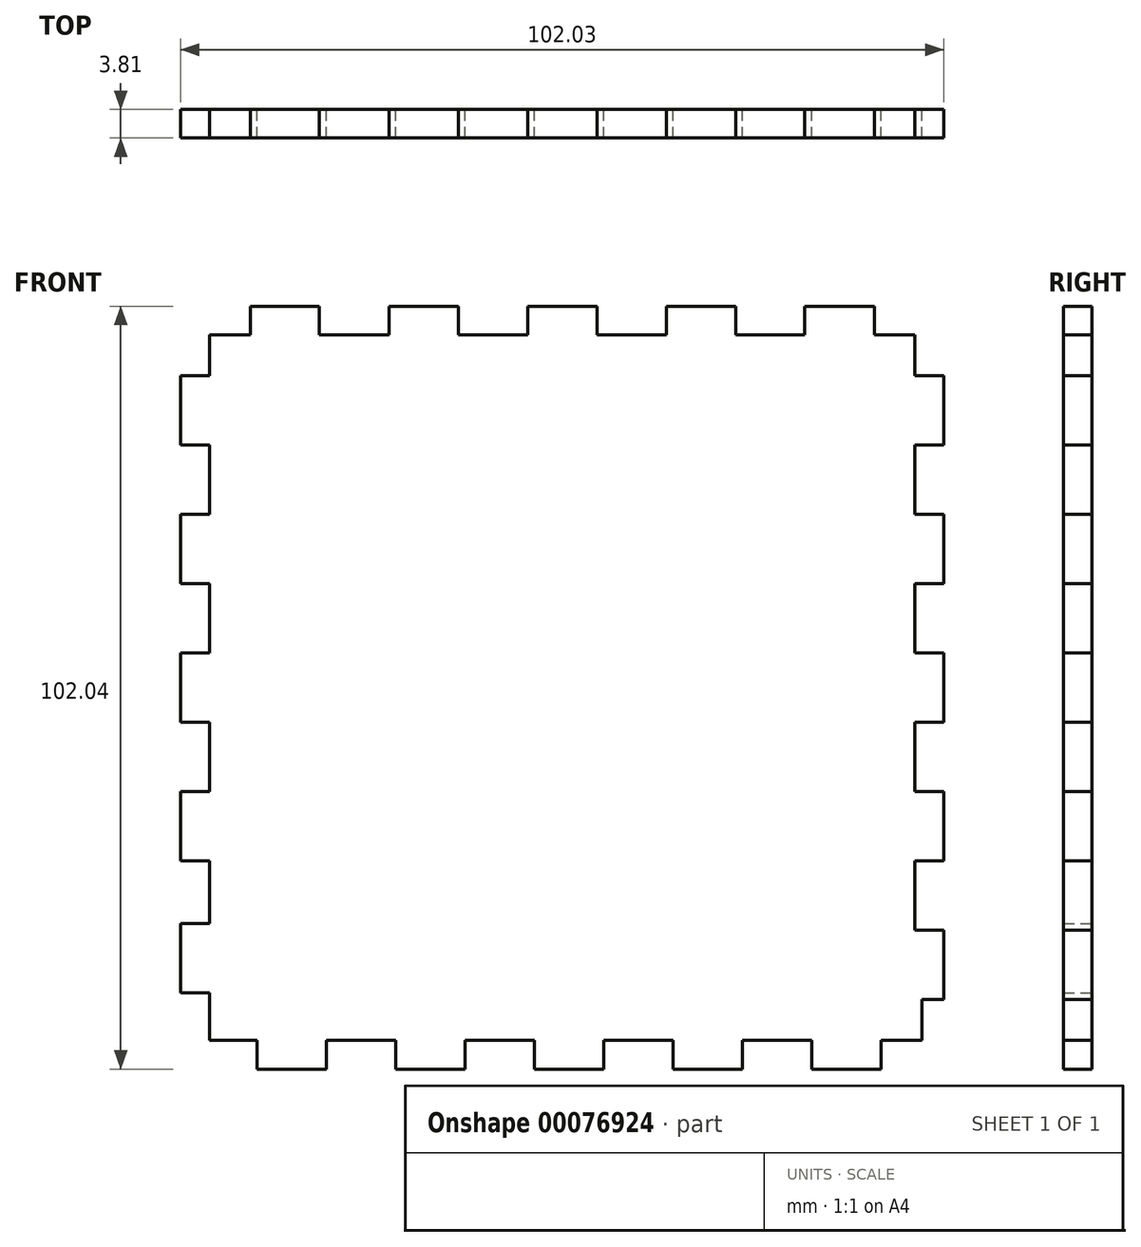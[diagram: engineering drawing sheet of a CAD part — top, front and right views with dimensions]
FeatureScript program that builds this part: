
annotation { "Feature Type Name" : "Feature", "Feature Type Description" : "" }
export const myFeature = defineFeature(function(context is Context, id is Id, definition is map)
    precondition{}
    {
        {
            var Q0;
            Q0=qCreatedBy(makeId("Front.planeOp"),FACE);
            var sketch = newSketch(context, id + "F0", { "sketchPlane" : qUnion([Q0])});
            skLineSegment(sketch, "E0.MirrorCS", {"start": v(-47.6, 5.44) * mm, "end": v(-51.43, 5.44) * mm});
            skLineSegment(sketch, "E1.MirrorCS", {"start": v(-51.43, -40) * mm, "end": v(-47.6, -40) * mm});
            skLineSegment(sketch, "E2.MirrorCS", {"start": v(-47.6, -30.73) * mm, "end": v(-51.43, -30.73) * mm});
            skLineSegment(sketch, "E3.MirrorCS", {"start": v(-51.43, -22.38) * mm, "end": v(-47.6, -22.38) * mm});
            skLineSegment(sketch, "E4.MirrorCS", {"start": v(-47.6, -13.1) * mm, "end": v(-51.43, -13.1) * mm});
            skLineSegment(sketch, "E5.MirrorCS", {"start": v(-51.43, -3.84) * mm, "end": v(-47.6, -3.84) * mm});
            skLineSegment(sketch, "E6.MirrorCS", {"start": v(-51.43, -13.1) * mm, "end": v(-51.43, -22.38) * mm});
            skLineSegment(sketch, "E7.MirrorCS", {"start": v(-47.6, -22.38) * mm, "end": v(-47.6, -30.73) * mm});
            skLineSegment(sketch, "E8.MirrorCS", {"start": v(-47.6, -40) * mm, "end": v(-47.6, -46.38) * mm});
            skLineSegment(sketch, "E9.MirrorCS", {"start": v(-51.43, -30.73) * mm, "end": v(-51.43, -40) * mm});
            skPoint(sketch, "E10.MirrorP", {"position": v(-51.43, -17.74) * mm});
            skLineSegment(sketch, "E11.MirrorCS", {"start": v(-47.6, -3.84) * mm, "end": v(-47.6, -13.1) * mm});
            skLineSegment(sketch, "E12.MirrorCS", {"start": v(-51.43, 5.44) * mm, "end": v(-51.43, -3.84) * mm});
            skLineSegment(sketch, "E13", {"start": v(-47.6, -46.38) * mm, "end": v(-41.22, -46.38) * mm});
            skLineSegment(sketch, "E14", {"start": v(-41.22, -46.38) * mm, "end": v(-41.22, -50.22) * mm});
            skLineSegment(sketch, "E15", {"start": v(-41.22, -50.22) * mm, "end": v(-31.95, -50.22) * mm});
            skLineSegment(sketch, "E16", {"start": v(-31.95, -50.22) * mm, "end": v(-31.95, -46.38) * mm});
            skLineSegment(sketch, "E17", {"start": v(-31.95, -46.38) * mm, "end": v(-22.68, -46.38) * mm});
            skLineSegment(sketch, "E18", {"start": v(-22.68, -46.38) * mm, "end": v(-22.68, -50.22) * mm});
            skLineSegment(sketch, "E19", {"start": v(-22.68, -50.22) * mm, "end": v(-13.4, -50.22) * mm});
            skLineSegment(sketch, "E20", {"start": v(-13.4, -50.22) * mm, "end": v(-13.4, -46.38) * mm});
            skLineSegment(sketch, "E21", {"start": v(-13.4, -46.38) * mm, "end": v(-4.13, -46.38) * mm});
            skLineSegment(sketch, "E22", {"start": v(-4.13, -46.38) * mm, "end": v(-4.13, -50.22) * mm});
            skLineSegment(sketch, "E23", {"start": v(-4.13, -50.22) * mm, "end": v(5.14, -50.22) * mm});
            skLineSegment(sketch, "E24", {"start": v(5.14, -50.22) * mm, "end": v(5.14, -46.38) * mm});
            skLineSegment(sketch, "E25", {"start": v(5.14, -46.38) * mm, "end": v(14.4, -46.38) * mm});
            skLineSegment(sketch, "E26", {"start": v(14.4, -46.38) * mm, "end": v(14.4, -50.22) * mm});
            skLineSegment(sketch, "E27", {"start": v(14.4, -50.22) * mm, "end": v(23.68, -50.22) * mm});
            skLineSegment(sketch, "E28", {"start": v(23.68, -50.22) * mm, "end": v(23.68, -46.38) * mm});
            skLineSegment(sketch, "E29", {"start": v(23.68, -46.38) * mm, "end": v(32.95, -46.38) * mm});
            skLineSegment(sketch, "E30", {"start": v(32.95, -46.38) * mm, "end": v(32.95, -50.22) * mm});
            skLineSegment(sketch, "E31", {"start": v(32.95, -50.22) * mm, "end": v(42.22, -50.22) * mm});
            skLineSegment(sketch, "E32", {"start": v(-47.6, 5.44) * mm, "end": v(-47.6, 14.7) * mm});
            skLineSegment(sketch, "E33", {"start": v(-47.6, 14.7) * mm, "end": v(-51.43, 14.7) * mm});
            skLineSegment(sketch, "E34", {"start": v(-51.43, 14.7) * mm, "end": v(-51.43, 23.98) * mm});
            skLineSegment(sketch, "E35", {"start": v(-51.43, 23.98) * mm, "end": v(-47.6, 23.98) * mm});
            skLineSegment(sketch, "E36", {"start": v(-47.6, 23.98) * mm, "end": v(-47.6, 33.25) * mm});
            skLineSegment(sketch, "E37", {"start": v(-47.6, 33.25) * mm, "end": v(-51.43, 33.25) * mm});
            skLineSegment(sketch, "E38", {"start": v(-51.43, 33.25) * mm, "end": v(-51.43, 42.52) * mm});
            skLineSegment(sketch, "E39", {"start": v(-51.43, 42.52) * mm, "end": v(-47.6, 42.52) * mm});
            skLineSegment(sketch, "E40", {"start": v(-47.6, 42.52) * mm, "end": v(-47.6, 47.98) * mm});
            skLineSegment(sketch, "E41", {"start": v(42.22, -50.22) * mm, "end": v(42.22, -46.38) * mm});
            skLineSegment(sketch, "E42", {"start": v(42.22, -46.38) * mm, "end": v(47.68, -46.38) * mm});
            skLineSegment(sketch, "E43", {"start": v(47.68, -46.38) * mm, "end": v(47.68, -40.92) * mm});
            skLineSegment(sketch, "E44", {"start": v(47.68, -40.92) * mm, "end": v(50.6, -40.92) * mm});
            skLineSegment(sketch, "E45", {"start": v(50.6, -40.92) * mm, "end": v(50.6, -31.65) * mm});
            skLineSegment(sketch, "E46", {"start": v(50.6, -31.65) * mm, "end": v(46.77, -31.65) * mm});
            skLineSegment(sketch, "E47", {"start": v(46.77, -31.65) * mm, "end": v(46.77, -22.38) * mm});
            skLineSegment(sketch, "E48", {"start": v(46.77, -22.38) * mm, "end": v(50.6, -22.38) * mm});
            skLineSegment(sketch, "E49", {"start": v(50.6, -22.38) * mm, "end": v(50.6, -13.1) * mm});
            skLineSegment(sketch, "E50", {"start": v(50.6, -13.1) * mm, "end": v(46.77, -13.1) * mm});
            skLineSegment(sketch, "E51", {"start": v(46.77, -13.1) * mm, "end": v(46.77, -3.84) * mm});
            skLineSegment(sketch, "E52", {"start": v(46.77, -3.84) * mm, "end": v(50.6, -3.84) * mm});
            skLineSegment(sketch, "E53", {"start": v(50.6, -3.84) * mm, "end": v(50.6, 5.44) * mm});
            skLineSegment(sketch, "E54", {"start": v(50.6, 5.44) * mm, "end": v(46.77, 5.44) * mm});
            skLineSegment(sketch, "E55", {"start": v(46.77, 5.44) * mm, "end": v(46.77, 14.7) * mm});
            skLineSegment(sketch, "E56", {"start": v(46.77, 14.7) * mm, "end": v(50.6, 14.7) * mm});
            skLineSegment(sketch, "E57", {"start": v(50.6, 14.7) * mm, "end": v(50.6, 23.98) * mm});
            skLineSegment(sketch, "E58", {"start": v(50.6, 23.98) * mm, "end": v(46.77, 23.98) * mm});
            skLineSegment(sketch, "E59", {"start": v(46.77, 23.98) * mm, "end": v(46.77, 33.25) * mm});
            skLineSegment(sketch, "E60", {"start": v(46.77, 33.25) * mm, "end": v(50.6, 33.25) * mm});
            skLineSegment(sketch, "E61", {"start": v(50.6, 33.25) * mm, "end": v(50.6, 42.52) * mm});
            skLineSegment(sketch, "E62", {"start": v(50.6, 42.52) * mm, "end": v(46.77, 42.52) * mm});
            skLineSegment(sketch, "E63", {"start": v(46.77, 42.52) * mm, "end": v(46.77, 47.98) * mm});
            skLineSegment(sketch, "E64", {"start": v(46.77, 47.98) * mm, "end": v(41.3, 47.98) * mm});
            skLineSegment(sketch, "E65", {"start": v(41.3, 47.98) * mm, "end": v(41.3, 51.82) * mm});
            skLineSegment(sketch, "E66", {"start": v(41.3, 51.82) * mm, "end": v(32.04, 51.82) * mm});
            skLineSegment(sketch, "E67", {"start": v(32.04, 51.82) * mm, "end": v(32.04, 47.98) * mm});
            skLineSegment(sketch, "E68", {"start": v(32.04, 47.98) * mm, "end": v(22.76, 47.98) * mm});
            skLineSegment(sketch, "E69", {"start": v(22.76, 47.98) * mm, "end": v(22.76, 51.82) * mm});
            skLineSegment(sketch, "E70", {"start": v(22.76, 51.82) * mm, "end": v(13.5, 51.82) * mm});
            skLineSegment(sketch, "E71", {"start": v(13.5, 51.82) * mm, "end": v(13.5, 47.98) * mm});
            skLineSegment(sketch, "E72", {"start": v(13.5, 47.98) * mm, "end": v(4.22, 47.98) * mm});
            skLineSegment(sketch, "E73", {"start": v(4.22, 47.98) * mm, "end": v(4.22, 51.82) * mm});
            skLineSegment(sketch, "E74", {"start": v(4.22, 51.82) * mm, "end": v(-5.05, 51.82) * mm});
            skLineSegment(sketch, "E75", {"start": v(-5.05, 51.82) * mm, "end": v(-5.05, 47.98) * mm});
            skLineSegment(sketch, "E76", {"start": v(-5.05, 47.98) * mm, "end": v(-14.32, 47.98) * mm});
            skLineSegment(sketch, "E77", {"start": v(-14.32, 47.98) * mm, "end": v(-14.32, 51.82) * mm});
            skLineSegment(sketch, "E78", {"start": v(-14.32, 51.82) * mm, "end": v(-23.6, 51.82) * mm});
            skLineSegment(sketch, "E79", {"start": v(-23.6, 51.82) * mm, "end": v(-23.6, 47.98) * mm});
            skLineSegment(sketch, "E80", {"start": v(-23.6, 47.98) * mm, "end": v(-32.86, 47.98) * mm});
            skLineSegment(sketch, "E81", {"start": v(-32.86, 47.98) * mm, "end": v(-32.86, 51.82) * mm});
            skLineSegment(sketch, "E82", {"start": v(-32.86, 51.82) * mm, "end": v(-42.13, 51.82) * mm});
            skLineSegment(sketch, "E83", {"start": v(-42.13, 51.82) * mm, "end": v(-42.13, 47.98) * mm});
            skLineSegment(sketch, "E84", {"start": v(-42.13, 47.98) * mm, "end": v(-47.6, 47.98) * mm});
            skSolve(sketch);
        }
        {
            var Q0;
            Q0=makeQuery(id+"F0.imprint","IMPRINT",FACE,{"disambiguationData":[TD([[makeQuery(id+"F0.imprint","IMPRINT",EDGE,{"derivedFrom":sQuery(id+"F0.wireOp",EDGE,"E0.MirrorCS")}),1.0]])]});
            extrude(context, id + "F1", {"entities" : qUnion([Q0]), "depth" : 3.8 * mm});
        }
    });
